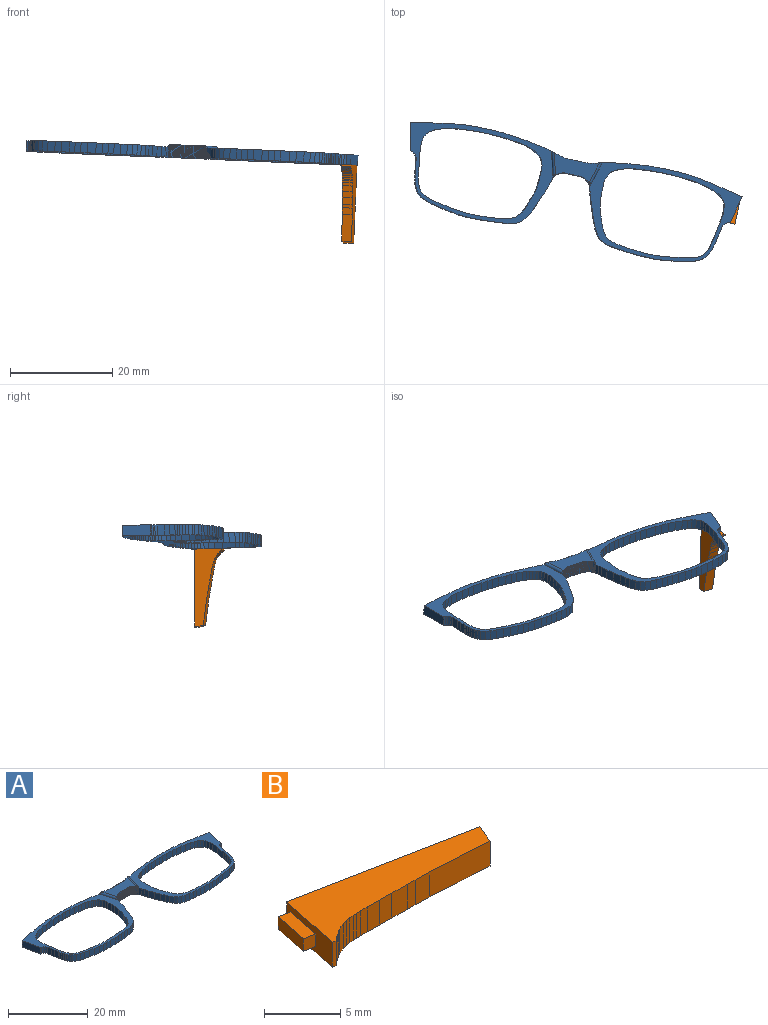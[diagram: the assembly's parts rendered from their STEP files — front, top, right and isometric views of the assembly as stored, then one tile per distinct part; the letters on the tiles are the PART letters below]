
ASSEMBLY  parts=2 mates=1
PART A: 350 faces, bbox 66.3x17.6x2.5 mm
  f0: plane 66.29x17.63mm, normal (0,0,-1), area 200.5mm2, adj f1,f2,f3,f4,f5,f6,f7,f8
  f1: plane 2x1.39mm, normal (-0.01,-1,0), area 2.8mm2, adj f0,f2,f131,f132
  f2: plane 2.04x2mm, normal (-0.04,-1,0), area 4.1mm2, adj f0,f1,f3,f132
  f3: plane 2x1.27mm, normal (-0.1,-1,0), area 2.6mm2, adj f0,f2,f4,f132
  f4: plane 2x1.46mm, normal (-0.11,-0.99,0), area 2.9mm2, adj f0,f3,f5,f132
  f5: plane 2x1.45mm, normal (-0.17,-0.99,0), area 2.9mm2, adj f0,f4,f6,f132
  f6: plane 2x1.39mm, normal (-0.24,-0.97,0), area 2.9mm2, adj f0,f5,f7,f132
  f7: plane 2x1.02mm, normal (-0.32,-0.95,0), area 2.2mm2, adj f0,f6,f8,f132
  f8: plane 2x0.81mm, normal (-0.39,-0.92,0), area 1.7mm2, adj f0,f7,f9,f132
  f9: plane 2x0.68mm, normal (-0.56,-0.83,0), area 1.6mm2, adj f0,f8,f10,f132
  f10: plane 2x0.59mm, normal (-0.69,-0.73,0), area 1.6mm2, adj f0,f9,f11,f132
  f11: plane 2x0.62mm, normal (-0.89,-0.45,0), area 1.4mm2, adj f0,f10,f12,f132
  f12: plane 2x0.77mm, normal (-0.98,-0.2,0), area 1.6mm2, adj f0,f11,f13,f132
  f13: plane 2x1.26mm, normal (-1,-0.06,0), area 2.5mm2, adj f0,f12,f14,f132
  f14: plane 2x1.76mm, normal (-0.99,0.13,0), area 3.5mm2, adj f0,f13,f15,f132
  f15: plane 2.51x2mm, normal (-0.99,0.16,0), area 5.1mm2, adj f0,f14,f16,f132
  f16: plane 2x0.96mm, normal (-0.99,0.15,0), area 1.9mm2, adj f0,f15,f17,f132
  f17: plane 2x0.91mm, normal (-0.99,0.17,0), area 1.8mm2, adj f0,f16,f18,f132
  f18: plane 2x1.12mm, normal (-0.96,0.3,0), area 2.4mm2, adj f0,f17,f19,f132
  f19: plane 2x0.81mm, normal (-0.91,0.41,0), area 1.8mm2, adj f0,f18,f20,f132
  f20: plane 2x0.65mm, normal (-0.78,0.63,0), area 1.7mm2, adj f0,f19,f21,f132
  f21: plane 2x0.59mm, normal (-0.57,0.82,0), area 1.4mm2, adj f0,f20,f22,f132
  f22: plane 2x0.68mm, normal (-0.41,0.91,0), area 1.5mm2, adj f0,f21,f23,f132
  f23: plane 2x1.21mm, normal (-0.25,0.97,0), area 2.5mm2, adj f0,f22,f24,f132
  f24: plane 2x1.07mm, normal (-0.19,0.98,0), area 2.2mm2, adj f0,f23,f25,f132
  f25: plane 2x1.25mm, normal (-0.18,0.98,0), area 2.5mm2, adj f0,f24,f26,f132
  f26: plane 2x1.29mm, normal (-0.17,0.98,0), area 2.6mm2, adj f0,f25,f27,f132
  f27: plane 2x1.25mm, normal (-0.11,0.99,0), area 2.5mm2, adj f0,f26,f28,f132
  f28: plane 2x1.24mm, normal (-0.11,0.99,0), area 2.5mm2, adj f0,f27,f29,f132
  f29: plane 2x0.89mm, normal (-0.05,1,0), area 1.8mm2, adj f0,f28,f30,f132
  f30: plane 2x1.3mm, normal (-0.02,1,0), area 2.6mm2, adj f0,f29,f31,f132
  f31: plane 2x1.49mm, normal (0.04,1,0), area 3mm2, adj f0,f30,f32,f132
  f32: plane 2x1.12mm, normal (0.08,1,0), area 2.2mm2, adj f0,f31,f33,f132
  f33: plane 2x1.21mm, normal (0.08,1,0), area 2.4mm2, adj f0,f32,f34,f132
  f34: plane 2x1.24mm, normal (0.12,0.99,0), area 2.5mm2, adj f0,f33,f35,f132
  f35: plane 2x1.01mm, normal (0.15,0.99,0), area 2mm2, adj f0,f34,f36,f132
  f36: plane 2x0.8mm, normal (0.25,0.97,0), area 1.6mm2, adj f0,f35,f37,f132
  f37: plane 2x0.67mm, normal (0.36,0.93,0), area 1.4mm2, adj f0,f36,f38,f132
  f38: plane 2x0.74mm, normal (0.48,0.88,0), area 1.7mm2, adj f0,f37,f39,f132
  f39: plane 2x0.46mm, normal (0.76,0.65,0), area 1.2mm2, adj f0,f38,f40,f132
  f40: plane 2x0.71mm, normal (0.8,0.59,0), area 1.8mm2, adj f0,f39,f41,f132
  f41: plane 2x0.84mm, normal (0.9,0.43,0), area 1.9mm2, adj f0,f40,f42,f132
  f42: plane 2x0.71mm, normal (0.93,0.36,0), area 1.5mm2, adj f0,f41,f43,f132
  f43: plane 2x0.9mm, normal (0.95,0.33,0), area 1.9mm2, adj f0,f42,f44,f132
  f44: plane 2x1.24mm, normal (0.94,0.33,0), area 2.6mm2, adj f0,f43,f45,f132
  f45: plane 2x1.25mm, normal (0.97,0.25,0), area 2.6mm2, adj f0,f44,f46,f132
  f46: plane 2x1.6mm, normal (1,0.09,0), area 3.2mm2, adj f0,f45,f47,f132
  f47: plane 2x1.15mm, normal (1,0.03,0), area 2.3mm2, adj f0,f46,f48,f132
  f48: plane 2x1.15mm, normal (1,0,0), area 2.3mm2, adj f0,f47,f49,f132
  f49: plane 2x0.81mm, normal (1,-0.08,0), area 1.6mm2, adj f0,f48,f50,f132
  f50: plane 2x0.84mm, normal (0.95,-0.32,0), area 1.8mm2, adj f0,f49,f51,f132
  f51: plane 2x0.56mm, normal (0.87,-0.49,0), area 1.3mm2, adj f0,f50,f52,f132
  f52: plane 2x0.43mm, normal (0.76,-0.65,0), area 1.1mm2, adj f0,f51,f53,f132
  f53: plane 2x0.39mm, normal (0.54,-0.84,0), area 0.9mm2, adj f0,f52,f54,f132
  f54: plane 2x0.54mm, normal (0.49,-0.87,0), area 1.2mm2, adj f0,f53,f55,f132
  f55: plane 2x0.56mm, normal (0.45,-0.89,0), area 1.2mm2, adj f0,f54,f56,f132
  f56: plane 2x0.56mm, normal (0.35,-0.94,0), area 1.2mm2, adj f0,f55,f57,f132
  f57: plane 2x0.87mm, normal (0.31,-0.95,0), area 1.8mm2, adj f0,f56,f58,f132
  f58: plane 2x1.24mm, normal (0.17,-0.99,0), area 2.5mm2, adj f0,f57,f59,f132
  f59: plane 2x1.06mm, normal (0.12,-0.99,0), area 2.1mm2, adj f0,f58,f60,f132
  f60: plane 2x1.14mm, normal (0.11,-0.99,0), area 2.3mm2, adj f0,f59,f61,f132
  f61: plane 2x1.58mm, normal (0.08,-1,0), area 3.2mm2, adj f0,f60,f62,f132
  f62: plane 2x1.36mm, normal (0.05,-1,0), area 2.7mm2, adj f0,f61,f131,f132
  f63: plane 2x0.74mm, normal (-0.97,-0.24,0), area 1.5mm2, adj f0,f64,f132,f308
  f64: plane 2x0.68mm, normal (-0.95,-0.3,0), area 1.4mm2, adj f0,f63,f65,f132
  f65: plane 2x1.27mm, normal (-0.95,-0.3,0), area 2.7mm2, adj f0,f64,f66,f132
  f66: plane 2x1.49mm, normal (-0.93,-0.37,0), area 3.2mm2, adj f0,f65,f67,f132
  f67: plane 2x1.58mm, normal (-0.94,-0.33,0), area 3.4mm2, adj f0,f66,f68,f132
  f68: plane 2x1.12mm, normal (-0.92,-0.38,0), area 2.4mm2, adj f0,f67,f69,f132
  f69: plane 2x0.96mm, normal (-0.91,-0.41,0), area 2.1mm2, adj f0,f68,f70,f132
  f70: plane 2x1.05mm, normal (-0.84,-0.54,0), area 2.5mm2, adj f0,f69,f71,f132
  f71: plane 2x0.7mm, normal (-0.75,-0.66,0), area 1.9mm2, adj f0,f70,f72,f132
  f72: plane 2x0.82mm, normal (-0.51,-0.86,0), area 1.9mm2, adj f0,f71,f73,f132
  f73: plane 2x1mm, normal (-0.31,-0.95,0), area 2.1mm2, adj f0,f72,f74,f132
  f74: plane 2x1.27mm, normal (-0.17,-0.99,0), area 2.6mm2, adj f0,f73,f75,f132
  f75: plane 2x1.28mm, normal (-0.1,-0.99,0), area 2.6mm2, adj f0,f74,f76,f132
  f76: plane 2x1.14mm, normal (-0.09,-1,0), area 2.3mm2, adj f0,f75,f77,f132
  f77: plane 2x1.18mm, normal (-0.07,-1,0), area 2.4mm2, adj f0,f76,f78,f132
  f78: plane 2x1.23mm, normal (-0.07,-1,0), area 2.5mm2, adj f0,f77,f79,f132
  f79: plane 2x1.68mm, normal (-0.02,-1,0), area 3.4mm2, adj f0,f78,f80,f132
  f80: plane 2x1.33mm, normal (0,-1,0), area 2.7mm2, adj f0,f79,f81,f132
  f81: plane 2x1.2mm, normal (0.06,-1,0), area 2.4mm2, adj f0,f80,f82,f132
  f82: plane 2x1.17mm, normal (0.13,-0.99,0), area 2.4mm2, adj f0,f81,f83,f132
  f83: plane 2x1.65mm, normal (0.13,-0.99,0), area 3.3mm2, adj f0,f82,f84,f132
  f84: plane 2x1.32mm, normal (0.19,-0.98,0), area 2.7mm2, adj f0,f83,f85,f132
  f85: plane 2x1.49mm, normal (0.2,-0.98,0), area 3mm2, adj f0,f84,f86,f132
  f86: plane 2x1.15mm, normal (0.27,-0.96,0), area 2.4mm2, adj f0,f85,f87,f132
  f87: plane 2x0.9mm, normal (0.37,-0.93,0), area 1.9mm2, adj f0,f86,f88,f132
  f88: plane 2x0.81mm, normal (0.54,-0.84,0), area 1.9mm2, adj f0,f87,f89,f132
  f89: plane 2x0.44mm, normal (0.73,-0.68,0), area 1.2mm2, adj f0,f88,f90,f132
  f90: plane 2x0.58mm, normal (0.83,-0.56,0), area 1.4mm2, adj f0,f89,f91,f132
  f91: plane 2x0.58mm, normal (0.9,-0.43,0), area 1.3mm2, adj f0,f90,f92,f132
  f92: plane 2x0.61mm, normal (0.93,-0.36,0), area 1.3mm2, adj f0,f91,f93,f132
  f93: plane 2x0.53mm, normal (0.98,-0.22,0), area 1.1mm2, adj f0,f92,f94,f132
  f94: plane 2x0.37mm, normal (0.98,-0.18,0), area 0.8mm2, adj f0,f93,f95,f132
  f95: plane 2x0.49mm, normal (0.99,-0.17,0), area 1mm2, adj f0,f94,f96,f132
  f96: plane 2x1.06mm, normal (0.98,-0.17,0), area 2.2mm2, adj f0,f95,f97,f132
  f97: plane 2x0.92mm, normal (0.99,-0.15,0), area 1.9mm2, adj f0,f96,f98,f132
  f98: plane 2x1.45mm, normal (0.98,-0.18,0), area 2.9mm2, adj f0,f97,f99,f132
  f99: plane 2x0.39mm, normal (0.84,-0.54,0), area 0.9mm2, adj f0,f98,f100,f132
  f100: plane 2x0.31mm, normal (0.71,-0.71,0), area 0.9mm2, adj f0,f99,f101,f132
  f101: plane 2x0.39mm, normal (0.51,-0.86,0), area 0.9mm2, adj f0,f100,f102,f132
  f102: plane 2x0.42mm, normal (0.24,-0.97,0), area 0.9mm2, adj f0,f101,f103,f132
  f103: plane 5.34x2mm, normal (0.98,-0.21,0), area 10.9mm2, adj f0,f102,f104,f132
  f104: plane 2x1.42mm, normal (0.2,0.98,0), area 2.9mm2, adj f0,f103,f105,f132
  f105: plane 2x1.56mm, normal (0.21,0.98,0), area 3.2mm2, adj f0,f104,f106,f132
  f106: plane 2x1.44mm, normal (0.18,0.98,0), area 2.9mm2, adj f0,f105,f107,f132
  f107: plane 2x1.07mm, normal (0.19,0.98,0), area 2.2mm2, adj f0,f106,f108,f132
  f108: plane 2x0.94mm, normal (0.17,0.98,0), area 1.9mm2, adj f0,f107,f109,f132
  f109: plane 2x0.72mm, normal (0.18,0.98,0), area 1.5mm2, adj f0,f108,f110,f132
  f110: plane 2x0.9mm, normal (0.18,0.98,0), area 1.8mm2, adj f0,f109,f111,f132
  f111: plane 2x0.85mm, normal (0.15,0.99,0), area 1.7mm2, adj f0,f110,f112,f132
  f112: plane 2x0.74mm, normal (0.15,0.99,0), area 1.5mm2, adj f0,f111,f113,f132
  f113: plane 2x0.63mm, normal (0.12,0.99,0), area 1.3mm2, adj f0,f112,f114,f132
  f114: plane 2x0.79mm, normal (0.07,1,0), area 1.6mm2, adj f0,f113,f115,f132
  f115: plane 2x1.79mm, normal (0.04,1,0), area 3.6mm2, adj f0,f114,f116,f132
  f116: plane 2x1.67mm, normal (0.01,1,0), area 3.3mm2, adj f0,f115,f117,f132
  f117: plane 2x1.15mm, normal (0.01,1,0), area 2.3mm2, adj f0,f116,f118,f132
  f118: plane 2x1.01mm, normal (-0.02,1,0), area 2mm2, adj f0,f117,f119,f132
  f119: plane 2x0.76mm, normal (-0.02,1,0), area 1.5mm2, adj f0,f118,f120,f132
  f120: plane 2x0.86mm, normal (-0.05,1,0), area 1.7mm2, adj f0,f119,f121,f132
  f121: plane 2x0.78mm, normal (-0.06,1,0), area 1.6mm2, adj f0,f120,f122,f132
  f122: plane 2x0.87mm, normal (-0.11,0.99,0), area 1.7mm2, adj f0,f121,f123,f132
  f123: plane 2x0.92mm, normal (-0.1,1,0), area 1.9mm2, adj f0,f122,f124,f132
  f124: plane 2x1.03mm, normal (-0.11,0.99,0), area 2.1mm2, adj f0,f123,f125,f132
  f125: plane 2x1.29mm, normal (-0.14,0.99,0), area 2.6mm2, adj f0,f124,f126,f132
  f126: plane 2x1.01mm, normal (-0.14,0.99,0), area 2mm2, adj f0,f125,f127,f132
  f127: plane 2x1.6mm, normal (-0.16,0.99,0), area 3.2mm2, adj f0,f126,f128,f132
  f128: plane 2x1.01mm, normal (-0.18,0.98,0), area 2.1mm2, adj f0,f127,f129,f132
  f129: plane 2x0.83mm, normal (-0.2,0.98,0), area 1.7mm2, adj f0,f128,f130,f132
  f130: plane 2x0.44mm, normal (-0.32,0.95,0), area 0.9mm2, adj f0,f129,f132,f309
  f131: plane 2x1.11mm, normal (0.02,-1,0), area 2.2mm2, adj f0,f1,f62,f132
  f132: plane 29.43x17.63mm, normal (0,0,1), area 88.3mm2, adj f1,f2,f3,f4,f5,f6,f7,f8
  f133: plane 2x0.74mm, normal (0.97,-0.24,0), area 1.5mm2, adj f0,f263,f264,f267
  f134: plane 2x0.44mm, normal (0.32,0.95,0), area 0.9mm2, adj f0,f135,f264,f266
  f135: plane 2x0.83mm, normal (0.2,0.98,0), area 1.7mm2, adj f0,f134,f136,f264
  f136: plane 2x1.01mm, normal (0.18,0.98,0), area 2.1mm2, adj f0,f135,f137,f264
  f137: plane 2x1.6mm, normal (0.16,0.99,0), area 3.2mm2, adj f0,f136,f138,f264
  f138: plane 2x1.01mm, normal (0.14,0.99,0), area 2mm2, adj f0,f137,f139,f264
  f139: plane 2x1.29mm, normal (0.14,0.99,0), area 2.6mm2, adj f0,f138,f140,f264
  f140: plane 2x1.03mm, normal (0.11,0.99,0), area 2.1mm2, adj f0,f139,f141,f264
  f141: plane 2x0.92mm, normal (0.1,1,0), area 1.9mm2, adj f0,f140,f142,f264
  f142: plane 2x0.87mm, normal (0.11,0.99,0), area 1.7mm2, adj f0,f141,f143,f264
  f143: plane 2x0.78mm, normal (0.06,1,0), area 1.6mm2, adj f0,f142,f144,f264
  f144: plane 2x0.86mm, normal (0.05,1,0), area 1.7mm2, adj f0,f143,f145,f264
  f145: plane 2x0.76mm, normal (0.02,1,0), area 1.5mm2, adj f0,f144,f146,f264
  f146: plane 2x1.01mm, normal (0.02,1,0), area 2mm2, adj f0,f145,f147,f264
  f147: plane 2x1.15mm, normal (-0.01,1,0), area 2.3mm2, adj f0,f146,f148,f264
  f148: plane 2x1.67mm, normal (-0.01,1,0), area 3.3mm2, adj f0,f147,f149,f264
  f149: plane 2x1.79mm, normal (-0.04,1,0), area 3.6mm2, adj f0,f148,f150,f264
  f150: plane 2x0.79mm, normal (-0.07,1,0), area 1.6mm2, adj f0,f149,f151,f264
  f151: plane 2x0.63mm, normal (-0.12,0.99,0), area 1.3mm2, adj f0,f150,f152,f264
  f152: plane 2x0.74mm, normal (-0.15,0.99,0), area 1.5mm2, adj f0,f151,f153,f264
  f153: plane 2x0.85mm, normal (-0.15,0.99,0), area 1.7mm2, adj f0,f152,f154,f264
  f154: plane 2x0.9mm, normal (-0.18,0.98,0), area 1.8mm2, adj f0,f153,f155,f264
  f155: plane 2x0.72mm, normal (-0.18,0.98,0), area 1.5mm2, adj f0,f154,f156,f264
  f156: plane 2x0.94mm, normal (-0.17,0.98,0), area 1.9mm2, adj f0,f155,f157,f264
  f157: plane 2x1.07mm, normal (-0.19,0.98,0), area 2.2mm2, adj f0,f156,f158,f264
  f158: plane 2x1.44mm, normal (-0.18,0.98,0), area 2.9mm2, adj f0,f157,f159,f264
  f159: plane 2x1.56mm, normal (-0.21,0.98,0), area 3.2mm2, adj f0,f158,f160,f264
  f160: plane 2x1.42mm, normal (-0.2,0.98,0), area 2.9mm2, adj f0,f159,f161,f264
  f161: plane 5.34x2mm, normal (-0.98,-0.21,0), area 10.9mm2, adj f0,f160,f162,f264
  f162: plane 2x0.42mm, normal (-0.24,-0.97,0), area 0.9mm2, adj f0,f161,f163,f264
  f163: plane 2x0.39mm, normal (-0.51,-0.86,0), area 0.9mm2, adj f0,f162,f164,f264
  f164: plane 2x0.31mm, normal (-0.71,-0.71,0), area 0.9mm2, adj f0,f163,f165,f264
  f165: plane 2x0.39mm, normal (-0.84,-0.54,0), area 0.9mm2, adj f0,f164,f166,f264
  f166: plane 2x1.45mm, normal (-0.98,-0.18,0), area 2.9mm2, adj f0,f165,f167,f264
  f167: plane 2x0.92mm, normal (-0.99,-0.15,0), area 1.9mm2, adj f0,f166,f168,f264
  f168: plane 2x1.06mm, normal (-0.98,-0.17,0), area 2.2mm2, adj f0,f167,f169,f264
  f169: plane 2x0.49mm, normal (-0.99,-0.17,0), area 1mm2, adj f0,f168,f170,f264
  f170: plane 2x0.37mm, normal (-0.98,-0.18,0), area 0.8mm2, adj f0,f169,f171,f264
  f171: plane 2x0.53mm, normal (-0.98,-0.22,0), area 1.1mm2, adj f0,f170,f172,f264
  f172: plane 2x0.61mm, normal (-0.93,-0.36,0), area 1.3mm2, adj f0,f171,f173,f264
  f173: plane 2x0.58mm, normal (-0.9,-0.43,0), area 1.3mm2, adj f0,f172,f174,f264
  f174: plane 2x0.58mm, normal (-0.83,-0.56,0), area 1.4mm2, adj f0,f173,f175,f264
  f175: plane 2x0.44mm, normal (-0.73,-0.68,0), area 1.2mm2, adj f0,f174,f176,f264
  f176: plane 2x0.81mm, normal (-0.54,-0.84,0), area 1.9mm2, adj f0,f175,f177,f264
  f177: plane 2x0.9mm, normal (-0.37,-0.93,0), area 1.9mm2, adj f0,f176,f178,f264
  f178: plane 2x1.15mm, normal (-0.27,-0.96,0), area 2.4mm2, adj f0,f177,f179,f264
  f179: plane 2x1.49mm, normal (-0.2,-0.98,0), area 3mm2, adj f0,f178,f180,f264
  f180: plane 2x1.32mm, normal (-0.19,-0.98,0), area 2.7mm2, adj f0,f179,f181,f264
  f181: plane 2x1.65mm, normal (-0.13,-0.99,0), area 3.3mm2, adj f0,f180,f182,f264
  f182: plane 2x1.17mm, normal (-0.13,-0.99,0), area 2.4mm2, adj f0,f181,f183,f264
  f183: plane 2x1.2mm, normal (-0.06,-1,0), area 2.4mm2, adj f0,f182,f184,f264
  f184: plane 2x1.33mm, normal (0,-1,0), area 2.7mm2, adj f0,f183,f185,f264
  f185: plane 2x1.68mm, normal (0.02,-1,0), area 3.4mm2, adj f0,f184,f186,f264
  f186: plane 2x1.23mm, normal (0.07,-1,0), area 2.5mm2, adj f0,f185,f187,f264
  f187: plane 2x1.18mm, normal (0.07,-1,0), area 2.4mm2, adj f0,f186,f188,f264
  f188: plane 2x1.14mm, normal (0.09,-1,0), area 2.3mm2, adj f0,f187,f189,f264
  f189: plane 2x1.28mm, normal (0.1,-0.99,0), area 2.6mm2, adj f0,f188,f190,f264
  f190: plane 2x1.27mm, normal (0.17,-0.99,0), area 2.6mm2, adj f0,f189,f191,f264
  f191: plane 2x1mm, normal (0.31,-0.95,0), area 2.1mm2, adj f0,f190,f192,f264
  f192: plane 2x0.82mm, normal (0.51,-0.86,0), area 1.9mm2, adj f0,f191,f193,f264
  f193: plane 2x0.7mm, normal (0.75,-0.66,0), area 1.9mm2, adj f0,f192,f194,f264
  f194: plane 2x1.05mm, normal (0.84,-0.54,0), area 2.5mm2, adj f0,f193,f195,f264
  f195: plane 2x0.96mm, normal (0.91,-0.41,0), area 2.1mm2, adj f0,f194,f196,f264
  f196: plane 2x1.12mm, normal (0.92,-0.38,0), area 2.4mm2, adj f0,f195,f197,f264
  f197: plane 2x1.58mm, normal (0.94,-0.33,0), area 3.4mm2, adj f0,f196,f198,f264
  f198: plane 2x1.49mm, normal (0.93,-0.37,0), area 3.2mm2, adj f0,f197,f199,f264
  f199: plane 2x1.27mm, normal (0.95,-0.3,0), area 2.7mm2, adj f0,f198,f263,f264
  f200: plane 2x1.15mm, normal (-1,0,0), area 2.3mm2, adj f0,f201,f262,f264
  f201: plane 2x1.15mm, normal (-1,0.03,0), area 2.3mm2, adj f0,f200,f202,f264
  f202: plane 2x1.6mm, normal (-1,0.09,0), area 3.2mm2, adj f0,f201,f203,f264
  f203: plane 2x1.25mm, normal (-0.97,0.25,0), area 2.6mm2, adj f0,f202,f204,f264
  f204: plane 2x1.24mm, normal (-0.94,0.33,0), area 2.6mm2, adj f0,f203,f205,f264
  f205: plane 2x0.9mm, normal (-0.95,0.33,0), area 1.9mm2, adj f0,f204,f206,f264
  f206: plane 2x0.71mm, normal (-0.93,0.36,0), area 1.5mm2, adj f0,f205,f207,f264
  f207: plane 2x0.84mm, normal (-0.9,0.43,0), area 1.9mm2, adj f0,f206,f208,f264
  f208: plane 2x0.71mm, normal (-0.8,0.59,0), area 1.8mm2, adj f0,f207,f209,f264
  f209: plane 2x0.46mm, normal (-0.76,0.65,0), area 1.2mm2, adj f0,f208,f210,f264
  f210: plane 2x0.74mm, normal (-0.48,0.88,0), area 1.7mm2, adj f0,f209,f211,f264
  f211: plane 2x0.67mm, normal (-0.36,0.93,0), area 1.4mm2, adj f0,f210,f212,f264
  f212: plane 2x0.8mm, normal (-0.25,0.97,0), area 1.6mm2, adj f0,f211,f213,f264
  f213: plane 2x1.01mm, normal (-0.15,0.99,0), area 2mm2, adj f0,f212,f214,f264
  f214: plane 2x1.24mm, normal (-0.12,0.99,0), area 2.5mm2, adj f0,f213,f215,f264
  f215: plane 2x1.21mm, normal (-0.08,1,0), area 2.4mm2, adj f0,f214,f216,f264
  f216: plane 2x1.12mm, normal (-0.08,1,0), area 2.2mm2, adj f0,f215,f217,f264
  f217: plane 2x1.49mm, normal (-0.04,1,0), area 3mm2, adj f0,f216,f218,f264
  f218: plane 2x1.3mm, normal (0.02,1,0), area 2.6mm2, adj f0,f217,f219,f264
  f219: plane 2x0.89mm, normal (0.05,1,0), area 1.8mm2, adj f0,f218,f220,f264
  f220: plane 2x1.24mm, normal (0.11,0.99,0), area 2.5mm2, adj f0,f219,f221,f264
  f221: plane 2x1.25mm, normal (0.11,0.99,0), area 2.5mm2, adj f0,f220,f222,f264
  f222: plane 2x1.29mm, normal (0.17,0.98,0), area 2.6mm2, adj f0,f221,f223,f264
  f223: plane 2x1.25mm, normal (0.18,0.98,0), area 2.5mm2, adj f0,f222,f224,f264
  f224: plane 2x1.07mm, normal (0.19,0.98,0), area 2.2mm2, adj f0,f223,f225,f264
  f225: plane 2x1.21mm, normal (0.25,0.97,0), area 2.5mm2, adj f0,f224,f226,f264
  f226: plane 2x0.68mm, normal (0.41,0.91,0), area 1.5mm2, adj f0,f225,f227,f264
  f227: plane 2x0.59mm, normal (0.57,0.82,0), area 1.4mm2, adj f0,f226,f228,f264
  f228: plane 2x0.65mm, normal (0.78,0.63,0), area 1.7mm2, adj f0,f227,f229,f264
  f229: plane 2x0.81mm, normal (0.91,0.41,0), area 1.8mm2, adj f0,f228,f230,f264
  f230: plane 2x1.12mm, normal (0.96,0.3,0), area 2.4mm2, adj f0,f229,f231,f264
  f231: plane 2x0.91mm, normal (0.99,0.17,0), area 1.8mm2, adj f0,f230,f232,f264
  f232: plane 2x0.96mm, normal (0.99,0.15,0), area 1.9mm2, adj f0,f231,f233,f264
  f233: plane 2.51x2mm, normal (0.99,0.16,0), area 5.1mm2, adj f0,f232,f234,f264
  f234: plane 2x1.76mm, normal (0.99,0.13,0), area 3.5mm2, adj f0,f233,f235,f264
  f235: plane 2x1.26mm, normal (1,-0.06,0), area 2.5mm2, adj f0,f234,f236,f264
  f236: plane 2x0.77mm, normal (0.98,-0.2,0), area 1.6mm2, adj f0,f235,f237,f264
  f237: plane 2x0.62mm, normal (0.89,-0.45,0), area 1.4mm2, adj f0,f236,f238,f264
  f238: plane 2x0.59mm, normal (0.69,-0.73,0), area 1.6mm2, adj f0,f237,f239,f264
  f239: plane 2x0.68mm, normal (0.56,-0.83,0), area 1.6mm2, adj f0,f238,f240,f264
  f240: plane 2x0.81mm, normal (0.39,-0.92,0), area 1.7mm2, adj f0,f239,f241,f264
  f241: plane 2x1.02mm, normal (0.32,-0.95,0), area 2.2mm2, adj f0,f240,f242,f264
  f242: plane 2x1.39mm, normal (0.24,-0.97,0), area 2.9mm2, adj f0,f241,f243,f264
  f243: plane 2x1.45mm, normal (0.17,-0.99,0), area 2.9mm2, adj f0,f242,f244,f264
  f244: plane 2x1.46mm, normal (0.11,-0.99,0), area 2.9mm2, adj f0,f243,f245,f264
  f245: plane 2x1.27mm, normal (0.1,-1,0), area 2.6mm2, adj f0,f244,f246,f264
  f246: plane 2.04x2mm, normal (0.04,-1,0), area 4.1mm2, adj f0,f245,f247,f264
  f247: plane 2x1.39mm, normal (0.01,-1,0), area 2.8mm2, adj f0,f246,f248,f264
  f248: plane 2x1.11mm, normal (-0.02,-1,0), area 2.2mm2, adj f0,f247,f249,f264
  f249: plane 2x1.36mm, normal (-0.05,-1,0), area 2.7mm2, adj f0,f248,f250,f264
  f250: plane 2x1.58mm, normal (-0.08,-1,0), area 3.2mm2, adj f0,f249,f251,f264
  f251: plane 2x1.14mm, normal (-0.11,-0.99,0), area 2.3mm2, adj f0,f250,f252,f264
  f252: plane 2x1.06mm, normal (-0.12,-0.99,0), area 2.1mm2, adj f0,f251,f253,f264
  f253: plane 2x1.24mm, normal (-0.17,-0.99,0), area 2.5mm2, adj f0,f252,f254,f264
  f254: plane 2x0.87mm, normal (-0.31,-0.95,0), area 1.8mm2, adj f0,f253,f255,f264
  f255: plane 2x0.56mm, normal (-0.35,-0.94,0), area 1.2mm2, adj f0,f254,f256,f264
  f256: plane 2x0.56mm, normal (-0.45,-0.89,0), area 1.2mm2, adj f0,f255,f257,f264
  f257: plane 2x0.54mm, normal (-0.49,-0.87,0), area 1.2mm2, adj f0,f256,f258,f264
  f258: plane 2x0.39mm, normal (-0.54,-0.84,0), area 0.9mm2, adj f0,f257,f259,f264
  f259: plane 2x0.43mm, normal (-0.76,-0.65,0), area 1.1mm2, adj f0,f258,f260,f264
  f260: plane 2x0.56mm, normal (-0.87,-0.49,0), area 1.3mm2, adj f0,f259,f261,f264
  f261: plane 2x0.84mm, normal (-0.95,-0.32,0), area 1.8mm2, adj f0,f260,f262,f264
  f262: plane 2x0.81mm, normal (-1,-0.08,0), area 1.6mm2, adj f0,f200,f261,f264
  f263: plane 2x0.68mm, normal (0.95,-0.3,0), area 1.4mm2, adj f0,f133,f199,f264
  f264: plane 29.43x17.63mm, normal (0,0,1), area 88.3mm2, adj f133,f134,f135,f136,f137,f138,f139,f140
  f265: plane 2.5x0.32mm, normal (0.26,0.97,0), area 0.8mm2, adj f0,f266,f334,f335
  f266: plane 2.5x1.41mm, normal (0.27,0.96,0), area 3.6mm2, adj f0,f134,f265,f335,f336
  f267: plane 2.33x0.23mm, normal (0.96,-0.29,0), area 0.5mm2, adj f0,f133,f268,f337
  f268: plane 2.45x0.2mm, normal (0.86,-0.5,0), area 0.5mm2, adj f0,f267,f269,f337
  f269: plane 2.5x0.19mm, normal (0.77,-0.64,0), area 0.6mm2, adj f0,f268,f270,f337
  f270: plane 2.5x0.21mm, normal (0.68,-0.73,0), area 0.7mm2, adj f0,f269,f271,f335,f337
  f271: plane 2.5x0.2mm, normal (0.59,-0.81,0), area 0.6mm2, adj f0,f270,f272,f335
  f272: plane 2.5x0.18mm, normal (0.55,-0.84,0), area 0.5mm2, adj f0,f271,f273,f335
  f273: plane 2.5x0.17mm, normal (0.54,-0.84,0), area 0.5mm2, adj f0,f272,f274,f335
  f274: plane 2.5x0.2mm, normal (0.47,-0.88,0), area 0.6mm2, adj f0,f273,f275,f335
  f275: plane 2.5x0.18mm, normal (0.36,-0.93,0), area 0.5mm2, adj f0,f274,f276,f335
  f276: plane 2.5x0.21mm, normal (0.43,-0.9,0), area 0.6mm2, adj f0,f275,f277,f335
  f277: plane 2.5x0.11mm, normal (0.21,-0.98,0), area 0.3mm2, adj f0,f276,f278,f335
  f278: plane 2.5x0.18mm, normal (0.09,-1,0), area 0.4mm2, adj f0,f277,f279,f335
  f279: plane 2.5x0.21mm, normal (0.15,-0.99,0), area 0.5mm2, adj f0,f278,f280,f335
  f280: plane 2.5x0.26mm, normal (0,-1,0), area 0.7mm2, adj f0,f279,f281,f335
  f281: plane 2.5x0.2mm, normal (-0.04,-1,0), area 0.5mm2, adj f0,f280,f282,f335
  f282: plane 2.5x0.32mm, normal (-0.02,-1,0), area 0.8mm2, adj f0,f281,f283,f335
  f283: plane 2.5x0.2mm, normal (-0.03,-1,0), area 0.5mm2, adj f0,f282,f284,f335
  f284: plane 2.5x0.15mm, normal (0,-1,0), area 0.4mm2, adj f0,f283,f285,f335
  f285: plane 2.5x0.21mm, normal (-0.02,-1,0), area 0.5mm2, adj f0,f284,f286,f335
  f286: plane 2.5x0.14mm, normal (-0.05,-1,0), area 0.3mm2, adj f0,f285,f287,f335
  f287: plane 2.5x0.05mm, normal (0.01,-1,0), area 0.1mm2, adj f0,f286,f288,f335
  f288: plane 2.5x0.05mm, normal (-0.01,-1,0), area 0.1mm2, adj f0,f287,f289,f335
  f289: plane 2.5x0.14mm, normal (0.05,-1,0), area 0.3mm2, adj f0,f288,f290,f335
  f290: plane 2.5x0.21mm, normal (0.02,-1,0), area 0.5mm2, adj f0,f289,f291,f335
  f291: plane 2.5x0.15mm, normal (0,-1,0), area 0.4mm2, adj f0,f290,f292,f335
  f292: plane 2.5x0.2mm, normal (0.03,-1,0), area 0.5mm2, adj f0,f291,f293,f335
  f293: plane 2.5x0.32mm, normal (0.02,-1,0), area 0.8mm2, adj f0,f292,f294,f335
  f294: plane 2.5x0.2mm, normal (0.04,-1,0), area 0.5mm2, adj f0,f293,f295,f335
  f295: plane 2.5x0.26mm, normal (0,-1,0), area 0.7mm2, adj f0,f294,f296,f335
  f296: plane 2.5x0.21mm, normal (-0.15,-0.99,0), area 0.5mm2, adj f0,f295,f297,f335
  f297: plane 2.5x0.18mm, normal (-0.09,-1,0), area 0.4mm2, adj f0,f296,f298,f335
  f298: plane 2.5x0.11mm, normal (-0.21,-0.98,0), area 0.3mm2, adj f0,f297,f299,f335
  f299: plane 2.5x0.21mm, normal (-0.43,-0.9,0), area 0.6mm2, adj f0,f298,f300,f335
  f300: plane 2.5x0.18mm, normal (-0.36,-0.93,0), area 0.5mm2, adj f0,f299,f301,f335
  f301: plane 2.5x0.2mm, normal (-0.47,-0.88,0), area 0.6mm2, adj f0,f300,f302,f335
  f302: plane 2.5x0.17mm, normal (-0.54,-0.84,0), area 0.5mm2, adj f0,f301,f303,f335
  f303: plane 2.5x0.18mm, normal (-0.55,-0.84,0), area 0.5mm2, adj f0,f302,f304,f335
  f304: plane 2.5x0.2mm, normal (-0.59,-0.81,0), area 0.6mm2, adj f0,f303,f305,f335
  f305: plane 2.5x0.21mm, normal (-0.68,-0.73,0), area 0.7mm2, adj f0,f304,f306,f335,f339
  f306: plane 2.5x0.19mm, normal (-0.77,-0.64,0), area 0.6mm2, adj f0,f305,f307,f339
  f307: plane 2.45x0.2mm, normal (-0.86,-0.5,0), area 0.5mm2, adj f0,f306,f308,f339
  f308: plane 2.33x0.23mm, normal (-0.96,-0.29,0), area 0.5mm2, adj f0,f63,f307,f339
  f309: plane 2.5x1.41mm, normal (-0.27,0.96,0), area 3.6mm2, adj f0,f130,f310,f335,f338
  f310: plane 2.5x0.32mm, normal (-0.26,0.97,0), area 0.8mm2, adj f0,f309,f311,f335
  f311: plane 2.5x0.35mm, normal (-0.2,0.98,0), area 0.9mm2, adj f0,f310,f312,f335
  f312: plane 2.5x0.23mm, normal (-0.23,0.97,0), area 0.6mm2, adj f0,f311,f313,f335
  f313: plane 2.5x0.28mm, normal (-0.19,0.98,0), area 0.7mm2, adj f0,f312,f314,f335
  f314: plane 2.5x0.36mm, normal (-0.13,0.99,0), area 0.9mm2, adj f0,f313,f315,f335
  f315: plane 2.5x0.43mm, normal (-0.02,1,0), area 1.1mm2, adj f0,f314,f316,f335
  f316: plane 2.5x0.29mm, normal (-0.03,1,0), area 0.7mm2, adj f0,f315,f317,f335
  f317: plane 2.5x0.29mm, normal (0.01,1,0), area 0.7mm2, adj f0,f316,f318,f335
  f318: plane 2.5x0.23mm, normal (0.03,1,0), area 0.6mm2, adj f0,f317,f319,f335
  f319: plane 2.5x0.21mm, normal (0.01,1,0), area 0.5mm2, adj f0,f318,f320,f335
  f320: plane 2.5x0.25mm, normal (0.03,1,0), area 0.6mm2, adj f0,f319,f321,f335
  f321: plane 2.5x0.26mm, normal (0.02,1,0), area 0.6mm2, adj f0,f320,f322,f335
  f322: plane 2.5x0.19mm, normal (-0.01,1,0), area 0.5mm2, adj f0,f321,f323,f335
  f323: plane 2.5x0.19mm, normal (0.01,1,0), area 0.5mm2, adj f0,f322,f324,f335
  f324: plane 2.5x0.26mm, normal (-0.02,1,0), area 0.6mm2, adj f0,f323,f325,f335
  f325: plane 2.5x0.25mm, normal (-0.03,1,0), area 0.6mm2, adj f0,f324,f326,f335
  f326: plane 2.5x0.21mm, normal (-0.01,1,0), area 0.5mm2, adj f0,f325,f327,f335
  f327: plane 2.5x0.23mm, normal (-0.03,1,0), area 0.6mm2, adj f0,f326,f328,f335
  f328: plane 2.5x0.29mm, normal (-0.01,1,0), area 0.7mm2, adj f0,f327,f329,f335
  f329: plane 2.5x0.29mm, normal (0.03,1,0), area 0.7mm2, adj f0,f328,f330,f335
  f330: plane 2.5x0.43mm, normal (0.02,1,0), area 1.1mm2, adj f0,f329,f331,f335
  f331: plane 2.5x0.36mm, normal (0.13,0.99,0), area 0.9mm2, adj f0,f330,f332,f335
  f332: plane 2.5x0.28mm, normal (0.19,0.98,0), area 0.7mm2, adj f0,f331,f333,f335
  f333: plane 2.5x0.23mm, normal (0.23,0.97,0), area 0.6mm2, adj f0,f332,f334,f335
  f334: plane 2.5x0.35mm, normal (0.2,0.98,0), area 0.9mm2, adj f0,f265,f333,f335
  f335: plane 9.06x4.27mm, normal (0,0,1), area 25mm2, adj f265,f266,f270,f271,f272,f273,f274,f275
  f336: cylinder r=0.5mm len=4.57mm, axis (-0.27,0.96,0), area 3.5mm2, adj f264,f266,f335,f337
  f337: cylinder r=0.5mm len=0.76mm, axis (-0.22,0.97,0), area 0.3mm2, adj f264,f267,f268,f269,f270,f335,f336
  f338: cylinder r=0.5mm len=4.57mm, axis (-0.27,-0.96,0), area 3.5mm2, adj f132,f309,f335,f339
  f339: cylinder r=0.5mm len=0.76mm, axis (-0.22,-0.97,0), area 0.3mm2, adj f132,f305,f306,f307,f308,f335,f338
  f340: plane 2.94x1mm, normal (0.98,0.2,0), area 3mm2, adj f0,f341,f343,f344
  f341: plane 1x0.98mm, normal (0.2,-0.98,0), area 1mm2, adj f0,f340,f342,f344
  f342: plane 2.94x1mm, normal (-0.98,-0.2,0), area 3mm2, adj f0,f341,f343,f344
  f343: plane 1x0.98mm, normal (-0.2,0.98,0), area 1mm2, adj f0,f340,f342,f344
  f344: plane 3.14x1.59mm, normal (0,0,-1), area 3mm2, adj f340,f341,f342,f343
  f345: plane 2.94x1mm, normal (-0.98,0.2,0), area 3mm2, adj f0,f346,f348,f349
  f346: plane 1x0.98mm, normal (0.2,0.98,0), area 1mm2, adj f0,f345,f347,f349
  f347: plane 2.94x1mm, normal (0.98,-0.2,0), area 3mm2, adj f0,f346,f348,f349
  f348: plane 1x0.98mm, normal (-0.2,-0.98,0), area 1mm2, adj f0,f345,f347,f349
  f349: plane 3.14x1.59mm, normal (0,0,-1), area 3mm2, adj f345,f346,f347,f348
PART B: 30 faces, bbox 16.6x5.4x2 mm
  f0: plane 2x0.3mm, normal (-0.19,-0.98,0), area 0.6mm2, adj f1,f22,f23,f24
  f1: plane 2x0.2mm, normal (0.66,-0.75,0), area 0.5mm2, adj f0,f2,f23,f24
  f2: plane 2x0.2mm, normal (0.59,-0.81,0), area 0.5mm2, adj f1,f3,f23,f24
  f3: plane 2x0.2mm, normal (0.57,-0.82,0), area 0.5mm2, adj f2,f4,f23,f24
  f4: plane 2x0.24mm, normal (0.57,-0.82,0), area 0.6mm2, adj f3,f5,f23,f24
  f5: plane 2x0.25mm, normal (0.5,-0.87,0), area 0.6mm2, adj f4,f6,f23,f24
  f6: plane 2x0.27mm, normal (0.45,-0.89,0), area 0.6mm2, adj f5,f7,f23,f24
  f7: plane 2x0.33mm, normal (0.39,-0.92,0), area 0.7mm2, adj f6,f8,f23,f24
  f8: plane 2x0.42mm, normal (0.25,-0.97,0), area 0.9mm2, adj f7,f9,f23,f24
  f9: plane 2x0.35mm, normal (0.14,-0.99,0), area 0.7mm2, adj f8,f10,f23,f24
  f10: plane 2x0.35mm, normal (0.1,-0.99,0), area 0.7mm2, adj f9,f11,f23,f24
  f11: plane 2x0.31mm, normal (0.06,-1,0), area 0.6mm2, adj f10,f12,f23,f24
  f12: plane 2x0.4mm, normal (0.03,-1,0), area 0.8mm2, adj f11,f13,f23,f24
  f13: plane 2x0.62mm, normal (0,-1,0), area 1.2mm2, adj f12,f14,f23,f24
  f14: plane 2x1.1mm, normal (-0.01,-1,0), area 2.2mm2, adj f13,f15,f23,f24
  f15: plane 2x1.14mm, normal (-0.02,-1,0), area 2.3mm2, adj f14,f16,f23,f24
  f16: plane 2x1.42mm, normal (-0.02,-1,0), area 2.8mm2, adj f15,f17,f23,f24
  f17: plane 2x0.7mm, normal (0,-1,0), area 1.4mm2, adj f16,f18,f23,f24
  f18: plane 2x1.34mm, normal (-0.03,-1,0), area 2.7mm2, adj f17,f19,f23,f24
  f19: plane 5.25x2mm, normal (-0.06,-1,0), area 10.5mm2, adj f18,f20,f23,f24
  f20: plane 2x1.62mm, normal (0.92,-0.38,0), area 3.5mm2, adj f19,f21,f23,f24
  f21: plane 14.95x2.92mm, normal (0.19,0.98,0), area 30.5mm2, adj f20,f22,f23,f24
  f22: plane 5.34x2mm, normal (-0.98,0.21,0), area 7.9mm2, adj f0,f21,f23,f24,f25,f26,f27,f28
  f23: plane 16.07x5.4mm, normal (0,0,1), area 44.5mm2, adj f0,f1,f2,f3,f4,f5,f6,f7
  f24: plane 16.07x5.4mm, normal (0,0,-1), area 44.5mm2, adj f0,f1,f2,f3,f4,f5,f6,f7
  f25: plane 3.14x1.59mm, normal (0,0,1), area 3mm2, adj f22,f26,f28,f29
  f26: plane 1x0.98mm, normal (0.21,0.98,0), area 1mm2, adj f22,f25,f27,f29
  f27: plane 3.14x1.59mm, normal (0,0,-1), area 3mm2, adj f22,f26,f28,f29
  f28: plane 1x0.98mm, normal (-0.21,-0.98,0), area 1mm2, adj f22,f25,f27,f29
  f29: plane 2.94x1mm, normal (-0.98,0.21,0), area 3mm2, adj f25,f26,f27,f28
PLACE A rot(axis=(-0.09,0.19,-0.98),12.9deg) t=(-6.31,6.59,3.49)mm
PLACE B rot(axis=(0.2,0.98,-0.02),92.4deg) t=(24.65,-5.99,49.64)mm
MATE fastened B.f29 <-> A.f349  axis (0.05,0.01,1) through (26.74,5.27,3)mm
